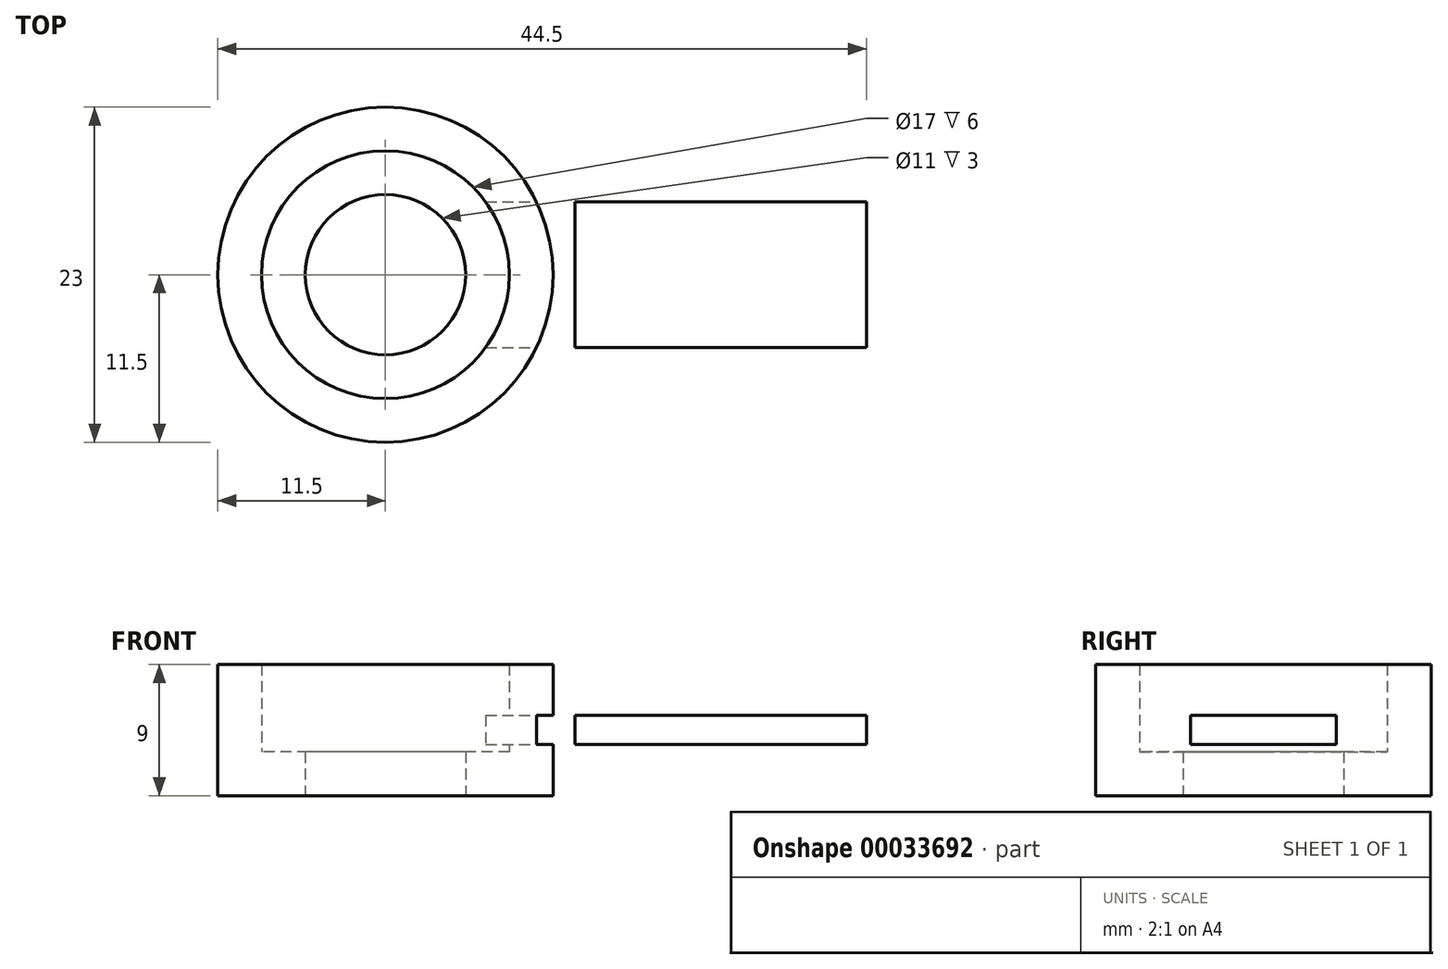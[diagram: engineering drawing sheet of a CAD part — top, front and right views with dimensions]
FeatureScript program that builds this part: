
annotation { "Feature Type Name" : "Feature", "Feature Type Description" : "" }
export const myFeature = defineFeature(function(context is Context, id is Id, definition is map)
    precondition{}
    {
        {
            var Q0;
            Q0=qCreatedBy(makeId("Top.planeOp"),FACE);
            var sketch = newSketch(context, id + "F0", { "sketchPlane" : qUnion([Q0])});
            skCircle(sketch, "E0", {"center": v(0, 0) * mm, "radius": 8.5 * mm});
            skCircle(sketch, "E1.0", {"center": v(0, 0) * mm, "radius": 11.5 * mm});
            skCircle(sketch, "E2.0", {"center": v(0, 0) * mm, "radius": 5.5 * mm});
            skLineSegment(sketch, "E3.bottom", {"start": v(0, 0) * mm, "end": v(-14.82, 0) * mm});
            skLineSegment(sketch, "E3.top", {"start": v(0, 0.75) * mm, "end": v(-14.82, 0.75) * mm});
            skLineSegment(sketch, "E3.left", {"start": v(0, 0) * mm, "end": v(0, 0.75) * mm});
            skLineSegment(sketch, "E3.right", {"start": v(-14.82, 0) * mm, "end": v(-14.82, 0.75) * mm});
            skSolve(sketch);
        }
        {
            var Q0;
            Q0=makeQuery(id+"F0.imprint","IMPRINT",FACE,{"disambiguationData":[TD([[makeQuery(id+"F0.imprint","IMPRINT",EDGE,{"derivedFrom":sQuery(id+"F0.wireOp",EDGE,"E0")}),1.0]])]});
            var Q1;
            Q1=makeQuery(id+"F0.imprint","IMPRINT",FACE,{"disambiguationData":[TD([[makeQuery(id+"F0.imprint","IMPRINT",EDGE,{"derivedFrom":sQuery(id+"F0.wireOp",EDGE,"E0")}),-1.0]])]});
            extrude(context, id + "F1", {"entities" : qUnion([Q0, Q1]), "depth" : 3 * mm});
        }
        {
            var Q0;
            Q0=makeQuery(id+"F0.imprint","IMPRINT",FACE,{"disambiguationData":[TD([[makeQuery(id+"F0.imprint","IMPRINT",EDGE,{"derivedFrom":sQuery(id+"F0.wireOp",EDGE,"E0")}),-1.0]])]});
            extrude(context, id + "F2", {"entities" : qUnion([Q0]), "operationType" : NewBodyOperationType.ADD, "depth" : 9 * mm});
        }
        {
            var Q0;
            Q0=qCreatedBy(makeId("Right.planeOp"),FACE);
            cPlane(context, id + "F3", {"entities" : qUnion([Q0]), "cplaneType" : CPlaneType.OFFSET, "offset" : 13 * mm, "width" : 150 * mm, "height" : 150 * mm});
        }
        {
            var Q0;
            Q0=qCreatedBy(id+"F3.planeOp",FACE);
            var sketch = newSketch(context, id + "F4", { "sketchPlane" : qUnion([Q0])});
            skLineSegment(sketch, "E4", {"start": v(0, 0) * mm, "end": v(0, 4.5) * mm, "construction": true});
            skLineSegment(sketch, "E5.rect.bottom", {"start": v(5, 5.5) * mm, "end": v(-5, 5.5) * mm});
            skLineSegment(sketch, "E5.rect.top", {"start": v(5, 3.5) * mm, "end": v(-5, 3.5) * mm});
            skLineSegment(sketch, "E5.rect.left", {"start": v(5, 5.5) * mm, "end": v(5, 3.5) * mm});
            skLineSegment(sketch, "E5.rect.right", {"start": v(-5, 5.5) * mm, "end": v(-5, 3.5) * mm});
            skPoint(sketch, "E5.rect.middle", {"position": v(0, 4.5) * mm});
            skSolve(sketch);
        }
        {
            var Q0;
            Q0=makeQuery(id+"F4.imprint","IMPRINT",FACE,{"disambiguationData":[TD([[makeQuery(id+"F4.imprint","IMPRINT",EDGE,{"derivedFrom":sQuery(id+"F4.wireOp",EDGE,"E5.rect.bottom")}),1.0]])]});
            extrude(context, id + "F5", {"entities" : qUnion([Q0]), "operationType" : NewBodyOperationType.REMOVE, "oppositeDirection" : true, "depth" : 12.2 * mm});
        }
        {
            var Q0;
            Q0=makeQuery(id+"F4.imprint","IMPRINT",FACE,{"disambiguationData":[TD([[makeQuery(id+"F4.imprint","IMPRINT",EDGE,{"derivedFrom":sQuery(id+"F4.wireOp",EDGE,"E5.rect.bottom")}),1.0]])]});
            extrude(context, id + "F6", {"entities" : qUnion([Q0]), "depth" : 20 * mm});
        }
    });
